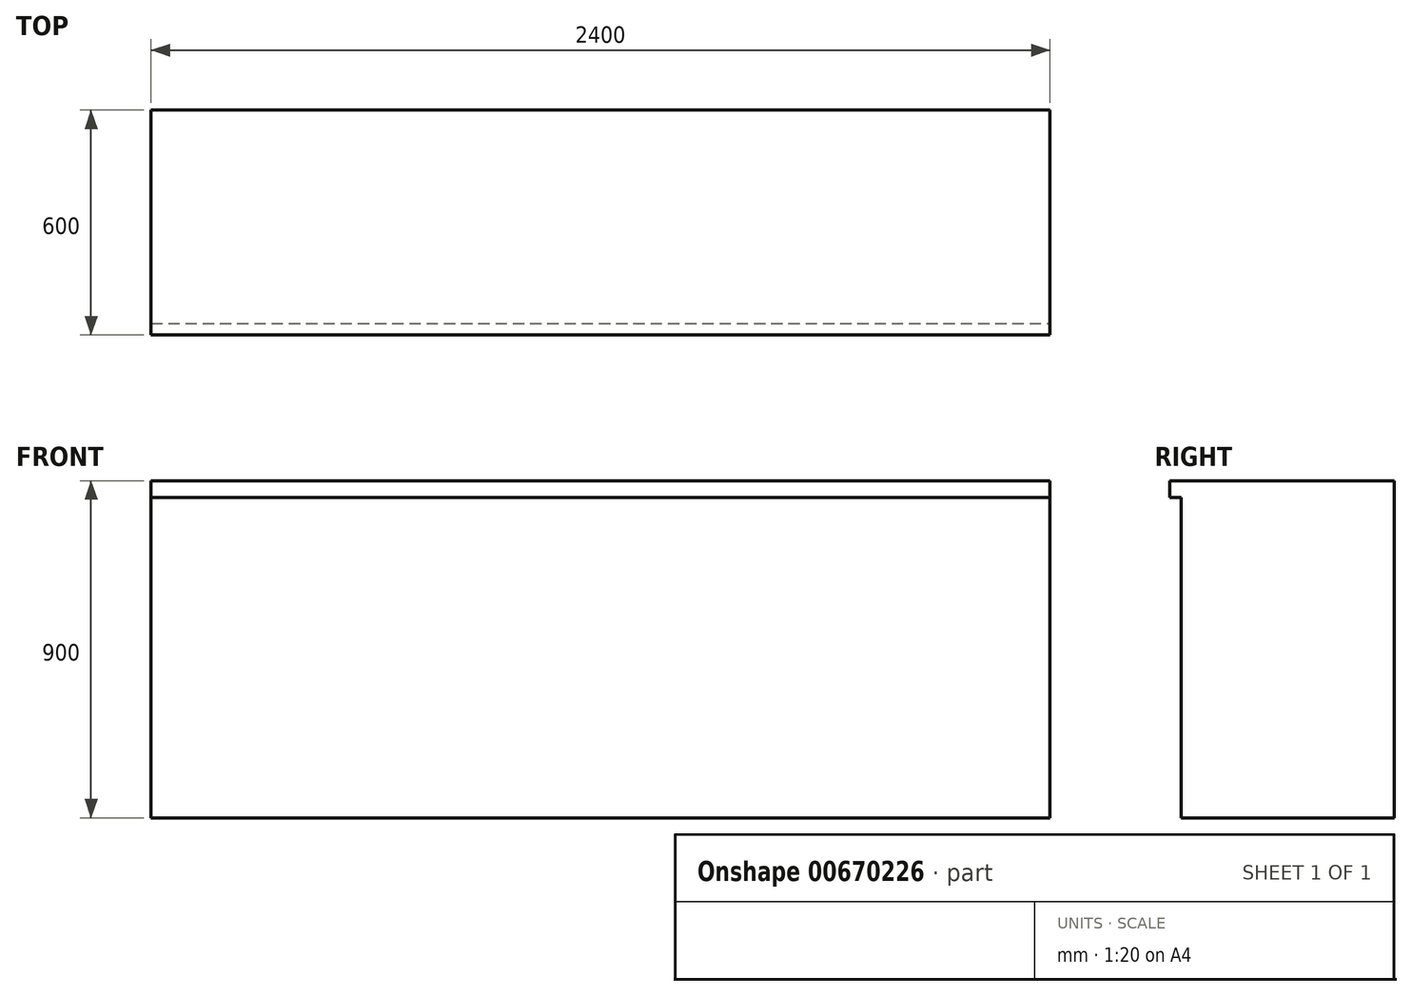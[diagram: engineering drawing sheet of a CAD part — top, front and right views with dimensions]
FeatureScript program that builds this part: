
annotation { "Feature Type Name" : "Feature", "Feature Type Description" : "" }
export const myFeature = defineFeature(function(context is Context, id is Id, definition is map)
    precondition{}
    {
        {
            var Q0;
            Q0=qCreatedBy(makeId("Front.planeOp"),FACE);
            var sketch = newSketch(context, id + "F0", { "sketchPlane" : qUnion([Q0])});
            skLineSegment(sketch, "E0.bottom", {"start": v(0, 0) * mm, "end": v(2400, 0) * mm, "construction": true});
            skLineSegment(sketch, "E0.top", {"start": v(0, 900) * mm, "end": v(2400, 900) * mm, "construction": true});
            skLineSegment(sketch, "E0.left", {"start": v(0, 0) * mm, "end": v(0, 900) * mm, "construction": true});
            skLineSegment(sketch, "E0.right", {"start": v(2400, 0) * mm, "end": v(2400, 900) * mm, "construction": true});
            skLineSegment(sketch, "E1", {"start": v(0, 856) * mm, "end": v(2400, 856) * mm, "construction": true});
            skLineSegment(sketch, "E2", {"start": v(0, 80) * mm, "end": v(2400, 80) * mm, "construction": true});
            skLineSegment(sketch, "E3", {"start": v(550, 856) * mm, "end": v(550, 80) * mm, "construction": true});
            skLineSegment(sketch, "E4", {"start": v(1145, 856) * mm, "end": v(1145, 80) * mm, "construction": true});
            skLineSegment(sketch, "E5", {"start": v(1495, 856) * mm, "end": v(1495, 80) * mm, "construction": true});
            skLineSegment(sketch, "E6", {"start": v(1805, 856) * mm, "end": v(1805, 80) * mm, "construction": true});
            skLineSegment(sketch, "E7", {"start": v(22, 856) * mm, "end": v(22, 80) * mm, "construction": true});
            skLineSegment(sketch, "E8", {"start": v(572, 856) * mm, "end": v(572, 80) * mm, "construction": true});
            skLineSegment(sketch, "E9", {"start": v(1123, 856) * mm, "end": v(1123, 80) * mm, "construction": true});
            skLineSegment(sketch, "E10", {"start": v(1517, 856) * mm, "end": v(1517, 80) * mm, "construction": true});
            skLineSegment(sketch, "E11.bottom", {"start": v(1145, 676) * mm, "end": v(1495, 676) * mm, "construction": true});
            skLineSegment(sketch, "E11.top", {"start": v(1145, 671) * mm, "end": v(1495, 671) * mm, "construction": true});
            skLineSegment(sketch, "E11.left", {"start": v(1145, 676) * mm, "end": v(1145, 671) * mm, "construction": true});
            skLineSegment(sketch, "E11.right", {"start": v(1495, 676) * mm, "end": v(1495, 671) * mm, "construction": true});
            skLineSegment(sketch, "E12.top", {"start": v(1145, 491) * mm, "end": v(1495, 491) * mm, "construction": true});
            skLineSegment(sketch, "E12.left", {"start": v(1145, 491) * mm, "end": v(1145, 468) * mm, "construction": true});
            skLineSegment(sketch, "E12.right", {"start": v(1495, 491) * mm, "end": v(1495, 468) * mm, "construction": true});
            skLineSegment(sketch, "E13.bottom", {"start": v(1145, 486) * mm, "end": v(1495, 486) * mm, "construction": true});
            skLineSegment(sketch, "E13.top", {"start": v(1145, 306) * mm, "end": v(1495, 306) * mm, "construction": true});
            skLineSegment(sketch, "E13.left", {"start": v(1145, 486) * mm, "end": v(1145, 306) * mm, "construction": true});
            skLineSegment(sketch, "E13.right", {"start": v(1495, 486) * mm, "end": v(1495, 306) * mm, "construction": true});
            skLineSegment(sketch, "E14", {"start": v(1145, 301) * mm, "end": v(1495, 301) * mm, "construction": true});
            skSolve(sketch);
        }
        {
            var Q0;
            Q0=qCreatedBy(makeId("Front.planeOp"),FACE);
            var sketch = newSketch(context, id + "F1", { "sketchPlane" : qUnion([Q0])});
            skLineSegment(sketch, "E15.bottom", {"start": v(0, 0) * mm, "end": v(2400, 0) * mm});
            skLineSegment(sketch, "E15.top", {"start": v(0, 900) * mm, "end": v(2400, 900) * mm});
            skLineSegment(sketch, "E15.left", {"start": v(0, 0) * mm, "end": v(0, 900) * mm});
            skLineSegment(sketch, "E15.right", {"start": v(2400, 0) * mm, "end": v(2400, 900) * mm});
            skSolve(sketch);
        }
        {
            var Q0;
            Q0 = qSketchRegion(id + "F1", true);
            extrude(context, id + "F2", {"entities" : qUnion([Q0]), "depth" : 600 * mm, "offsetDistance" : 25 * mm});
        }
        {
            var Q0;
            Q0=makeQuery(id+"F2.opExtrude","CAP_FACE",FACE,{"disambiguationData":[OSD([sQuery(id+"F1.wireOp",EDGE,"E15.bottom"),sQuery(id+"F1.wireOp",EDGE,"E15.top"),sQuery(id+"F1.wireOp",EDGE,"E15.left"),sQuery(id+"F1.wireOp",EDGE,"E15.right")])],"isStart":false});
            var sketch = newSketch(context, id + "F3", { "sketchPlane" : qUnion([Q0])});
            skLineSegment(sketch, "E16.bottom", {"start": v(0, 0) * mm, "end": v(2400, 0) * mm});
            skLineSegment(sketch, "E16.top", {"start": v(0, 856) * mm, "end": v(2400, 856) * mm});
            skLineSegment(sketch, "E16.left", {"start": v(0, 0) * mm, "end": v(0, 856) * mm});
            skLineSegment(sketch, "E16.right", {"start": v(2400, 0) * mm, "end": v(2400, 856) * mm});
            skSolve(sketch);
        }
        {
            var Q0;
            Q0 = qSketchRegion(id + "F3", true);
            extrude(context, id + "F4", {"entities" : qUnion([Q0]), "operationType" : NewBodyOperationType.REMOVE, "oppositeDirection" : true, "depth" : 30 * mm, "offsetDistance" : 25 * mm});
        }
    });
